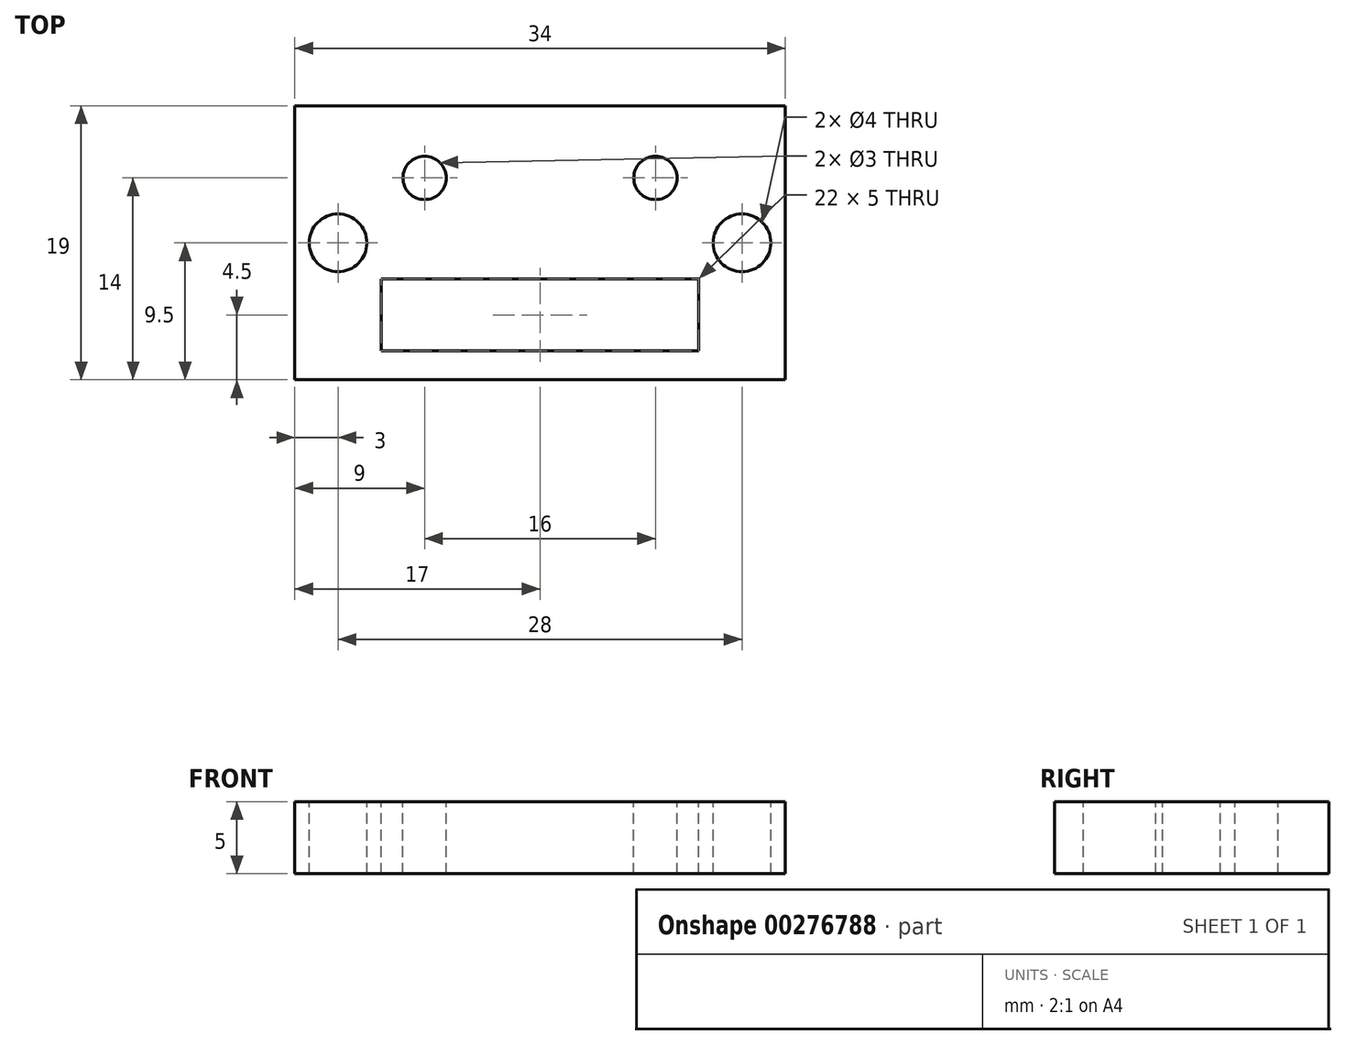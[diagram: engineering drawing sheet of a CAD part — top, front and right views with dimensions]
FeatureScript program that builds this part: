
annotation { "Feature Type Name" : "Feature", "Feature Type Description" : "" }
export const myFeature = defineFeature(function(context is Context, id is Id, definition is map)
    precondition{}
    {
        {
            var Q0;
            Q0=qCreatedBy(makeId("Top.planeOp"),FACE);
            var sketch = newSketch(context, id + "F0", { "sketchPlane" : qUnion([Q0])});
            skLineSegment(sketch, "E0.bottom", {"start": v(17, 9.5) * mm, "end": v(-17, 9.5) * mm});
            skLineSegment(sketch, "E0.top", {"start": v(17, -9.5) * mm, "end": v(-17, -9.5) * mm});
            skLineSegment(sketch, "E0.left", {"start": v(17, 9.5) * mm, "end": v(17, -9.5) * mm});
            skLineSegment(sketch, "E0.right", {"start": v(-17, 9.5) * mm, "end": v(-17, -9.5) * mm});
            skPoint(sketch, "E0.middle", {"position": v(0, 0) * mm});
            skLineSegment(sketch, "E1.left", {"start": v(17, -9.5) * mm, "end": v(17, -7.5) * mm});
            skLineSegment(sketch, "E2.left", {"start": v(-17, -9.5) * mm, "end": v(-17, -7.5) * mm});
            skLineSegment(sketch, "E2.right", {"start": v(-11, -9.5) * mm, "end": v(-11, -7.5) * mm});
            skLineSegment(sketch, "E3.bottom", {"start": v(-11, -7.5) * mm, "end": v(11, -7.5) * mm});
            skLineSegment(sketch, "E4.bottom", {"start": v(-17, -9.5) * mm, "end": v(-17, -9.5) * mm});
            skLineSegment(sketch, "E4.top", {"start": v(-17, 0) * mm, "end": v(-14, 0) * mm});
            skLineSegment(sketch, "E4.left", {"start": v(-17, -9.5) * mm, "end": v(-17, 0) * mm});
            skCircle(sketch, "E5", {"center": v(-14, 0) * mm, "radius": 2 * mm});
            skLineSegment(sketch, "E6.bottom", {"start": v(17, -9.5) * mm, "end": v(14, -9.5) * mm});
            skLineSegment(sketch, "E6.top", {"start": v(17, 0) * mm, "end": v(14, 0) * mm});
            skLineSegment(sketch, "E6.left", {"start": v(17, -9.5) * mm, "end": v(17, 0) * mm});
            skCircle(sketch, "E7", {"center": v(14, 0) * mm, "radius": 2 * mm});
            skLineSegment(sketch, "E8", {"start": v(-11, -7.5) * mm, "end": v(-11, -2.5) * mm});
            skLineSegment(sketch, "E9", {"start": v(11, -7.5) * mm, "end": v(11, -2.5) * mm});
            skLineSegment(sketch, "E10", {"start": v(11, -2.5) * mm, "end": v(-11, -2.5) * mm});
            skSolve(sketch);
        }
        {
            var Q0;
            Q0=makeQuery(id+"F0.imprint","IMPRINT",FACE,{"disambiguationData":[TD([[makeQuery(id+"F0.imprint","IMPRINT",EDGE,{"derivedFrom":sQuery(id+"F0.wireOp",EDGE,"E0.bottom")}),1.0]])]});
            extrude(context, id + "F1", {"entities" : qUnion([Q0]), "oppositeDirection" : true, "depth" : 5 * mm});
        }
        {
            var Q0;
            Q0=qCreatedBy(makeId("Top.planeOp"),FACE);
            var sketch = newSketch(context, id + "F2", { "sketchPlane" : qUnion([Q0])});
            skCircle(sketch, "E11", {"center": v(13, 0) * mm, "radius": 2 * mm});
            skSolve(sketch);
        }
        {
            var Q0;
            Q0=sQuery(id+"F2.wireOp",VERTEX,"E11.center");
            var Q1;
            Q1=makeQuery(id+"F1.opExtrude","SWEPT_BODY",BODY,{"disambiguationData":[OSD([sQuery(id+"F0.wireOp",EDGE,"E0.bottom"),sQuery(id+"F0.wireOp",EDGE,"E0.top"),sQuery(id+"F0.wireOp",EDGE,"E0.left"),sQuery(id+"F0.wireOp",EDGE,"E0.right")])]});
            hole(context, id + "F3", {"style" : HoleStyle.SIMPLE, "endStyle" : HoleEndStyle.THROUGH, "holeDiameter" : 4 * mm, "tappedDepth" : 12.7 * mm, "tapClearance" : 3, "locations" : qUnion([Q0]), "scope" : qUnion([Q1])});
        }
        {
            var Q0;
            Q0 = qSketchRegion(id + "F0", true);
            extrude(context, id + "F4", {"entities" : qUnion([Q0]), "operationType" : NewBodyOperationType.ADD, "oppositeDirection" : true, "depth" : 5 * mm});
        }
        {
            var Q0;
            {var subQ0=sQuery(id+"F0.wireOp",EDGE,"E10");var subQ1=sQuery(id+"F0.wireOp",EDGE,"E9");var subQ2=sQuery(id+"F0.wireOp",EDGE,"E8");var subQ3=sQuery(id+"F0.wireOp",EDGE,"E7");var subQ4=sQuery(id+"F0.wireOp",EDGE,"E6.left");var subQ5=sQuery(id+"F0.wireOp",EDGE,"E6.bottom");var subQ6=sQuery(id+"F0.wireOp",EDGE,"E5");var subQ7=sQuery(id+"F0.wireOp",EDGE,"E4.left");var subQ8=sQuery(id+"F0.wireOp",EDGE,"E3.bottom");var subQ9=sQuery(id+"F0.wireOp",EDGE,"E0.right");var subQ10=sQuery(id+"F0.wireOp",EDGE,"E0.left");var subQ11=sQuery(id+"F0.wireOp",EDGE,"E0.top");var subQ12=sQuery(id+"F0.wireOp",EDGE,"E0.bottom");Q0=makeQuery(id+"F4.boolean.opBoolean","MERGE",FACE,{"derivedFrom":[makeQuery(id+"F1.opExtrude","CAP_FACE",FACE,{"disambiguationData":[OSD([subQ12,subQ11,subQ10,subQ9,subQ8,subQ7,subQ6,subQ5,subQ4,subQ3,subQ2,subQ1,subQ0])],"isStart":true}),makeQuery(id+"F4.opExtrude","CAP_FACE",FACE,{"disambiguationData":[OSD([subQ12,subQ11,subQ10,subQ9,subQ8,subQ7,subQ6,subQ5,subQ4,subQ3,subQ2,subQ1,subQ0])],"isStart":true})]});}
            var sketch = newSketch(context, id + "F5", { "sketchPlane" : qUnion([Q0])});
            skCircle(sketch, "E12", {"center": v(-8, 4.5) * mm, "radius": 1.5 * mm});
            skCircle(sketch, "E13", {"center": v(8, 4.5) * mm, "radius": 1.5 * mm});
            skSolve(sketch);
        }
        {
            var Q0;
            Q0=sQuery(id+"F5.wireOp",VERTEX,"E12.center");
            var Q1;
            Q1=sQuery(id+"F5.wireOp",VERTEX,"E13.center");
            var Q2;
            Q2=makeQuery(id+"F1.opExtrude","SWEPT_BODY",BODY,{"disambiguationData":[OSD([sQuery(id+"F0.wireOp",EDGE,"E0.bottom"),sQuery(id+"F0.wireOp",EDGE,"E0.top"),sQuery(id+"F0.wireOp",EDGE,"E0.left"),sQuery(id+"F0.wireOp",EDGE,"E0.right"),sQuery(id+"F0.wireOp",EDGE,"E3.bottom"),sQuery(id+"F0.wireOp",EDGE,"E4.left"),sQuery(id+"F0.wireOp",EDGE,"E5"),sQuery(id+"F0.wireOp",EDGE,"E6.bottom"),sQuery(id+"F0.wireOp",EDGE,"E6.left"),sQuery(id+"F0.wireOp",EDGE,"E7"),sQuery(id+"F0.wireOp",EDGE,"E8"),sQuery(id+"F0.wireOp",EDGE,"E9"),sQuery(id+"F0.wireOp",EDGE,"E10")])]});
            hole(context, id + "F6", {"style" : HoleStyle.SIMPLE, "endStyle" : HoleEndStyle.THROUGH, "holeDiameter" : 3 * mm, "tappedDepth" : 12.7 * mm, "tapClearance" : 3, "locations" : qUnion([Q0, Q1]), "scope" : qUnion([Q2])});
        }
    });
